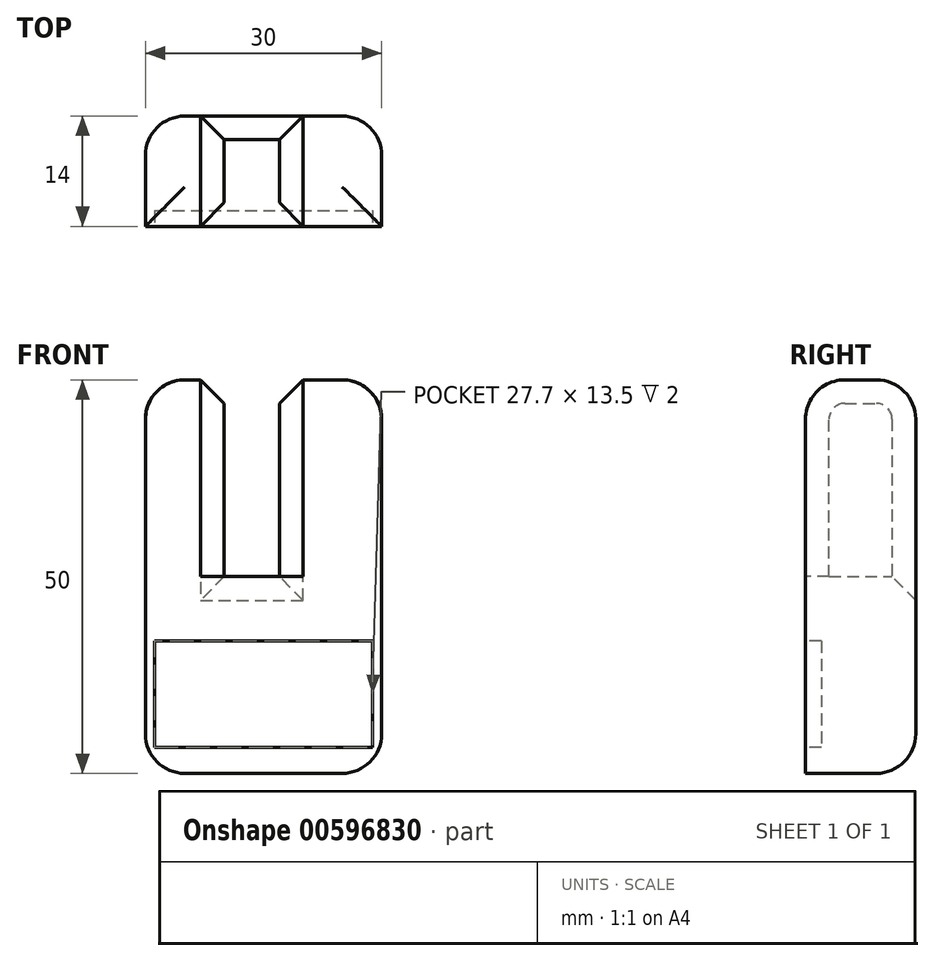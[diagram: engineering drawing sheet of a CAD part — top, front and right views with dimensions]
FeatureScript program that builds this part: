
annotation { "Feature Type Name" : "Feature", "Feature Type Description" : "" }
export const myFeature = defineFeature(function(context is Context, id is Id, definition is map)
    precondition{}
    {
        {
            var Q0;
            Q0=qCreatedBy(makeId("Front.planeOp"),FACE);
            var sketch = newSketch(context, id + "F0", { "sketchPlane" : qUnion([Q0])});
            skLineSegment(sketch, "E0.bottom", {"start": v(-13.28, -20.83) * mm, "end": v(16.72, -20.83) * mm});
            skLineSegment(sketch, "E0.top", {"start": v(-13.28, 29.17) * mm, "end": v(16.72, 29.17) * mm});
            skLineSegment(sketch, "E0.left", {"start": v(-13.28, -20.83) * mm, "end": v(-13.28, 29.17) * mm});
            skLineSegment(sketch, "E0.right", {"start": v(16.72, -20.83) * mm, "end": v(16.72, 29.17) * mm});
            skLineSegment(sketch, "E1.bottom", {"start": v(-3.28, 4.17) * mm, "end": v(3.73, 4.17) * mm});
            skLineSegment(sketch, "E1.top", {"start": v(-3.28, 29.17) * mm, "end": v(3.73, 29.17) * mm});
            skLineSegment(sketch, "E1.left", {"start": v(-3.28, 4.17) * mm, "end": v(-3.28, 29.17) * mm});
            skLineSegment(sketch, "E1.right", {"start": v(3.73, 4.17) * mm, "end": v(3.73, 29.17) * mm});
            skLineSegment(sketch, "E2.bottom", {"start": v(-12.13, -4.12) * mm, "end": v(15.57, -4.12) * mm});
            skLineSegment(sketch, "E2.top", {"start": v(-12.13, -17.62) * mm, "end": v(15.57, -17.62) * mm});
            skLineSegment(sketch, "E2.left", {"start": v(-12.13, -4.12) * mm, "end": v(-12.13, -17.62) * mm});
            skLineSegment(sketch, "E2.right", {"start": v(15.57, -4.12) * mm, "end": v(15.57, -17.62) * mm});
            skSolve(sketch);
        }
        {
            var Q0;
            Q0=makeQuery(id+"F0.imprint","IMPRINT",FACE,{"disambiguationData":[TD([[makeQuery(id+"F0.imprint","IMPRINT",EDGE,{"derivedFrom":sQuery(id+"F0.wireOp",EDGE,"E2.bottom")}),-1.0]])]});
            var Q1;
            Q1=makeQuery(id+"F0.imprint","IMPRINT",FACE,{"disambiguationData":[TD([[makeQuery(id+"F0.imprint","IMPRINT",EDGE,{"derivedFrom":sQuery(id+"F0.wireOp",EDGE,"E0.bottom")}),1.0]])]});
            extrude(context, id + "F1", {"entities" : qUnion([Q0, Q1]), "depth" : 14 * mm, "offsetDistance" : 25 * mm});
        }
        {
            var Q0;
            Q0=makeQuery(id+"F1.opExtrude","CAP_EDGE",EDGE,{"disambiguationData":[OSD([sQuery(id+"F0.wireOp",EDGE,"E0.bottom")])],"isStart":true});
            var Q1;
            Q1=makeQuery(id+"F1.opExtrude","CAP_EDGE",EDGE,{"disambiguationData":[OSD([sQuery(id+"F0.wireOp",EDGE,"E0.left")])],"isStart":true});
            var Q2;
            Q2=makeQuery(id+"F1.opExtrude","CAP_EDGE",EDGE,{"disambiguationData":[OSD([sQuery(id+"F0.wireOp",EDGE,"E0.right")])],"isStart":true});
            var Q3;
            Q3=makeQuery(id+"F1.opExtrude","SWEPT_EDGE",EDGE,{"disambiguationData":[OSD([sQuery(id+"F0.wireOp",EDGE,"E0.bottom"),sQuery(id+"F0.wireOp",EDGE,"E0.right")])]});
            var Q4;
            Q4=makeQuery(id+"F1.opExtrude","SWEPT_EDGE",EDGE,{"disambiguationData":[OSD([sQuery(id+"F0.wireOp",EDGE,"E0.bottom"),sQuery(id+"F0.wireOp",EDGE,"E0.left")])]});
            var Q5;
            {var subQ0=sQuery(id+"F0.wireOp",EDGE,"E0.top");Q5=makeQuery(id+"F1.opExtrude","CAP_EDGE",EDGE,{"disambiguationData":[OSD([subQ0]),TDD([makeQuery(id+"F0.imprint","IMPRINT",EDGE,{"disambiguationData":[TD([[makeQuery(id+"F0.imprint","INTERSECT",VERTEX,{"derivedFrom":[subQ0,sQuery(id+"F0.wireOp",EDGE,"E0.left")]}),-1.0]])],"derivedFrom":subQ0})])],"isStart":true});}
            var Q6;
            {var subQ0=sQuery(id+"F0.wireOp",EDGE,"E0.top");Q6=makeQuery(id+"F1.opExtrude","CAP_EDGE",EDGE,{"disambiguationData":[OSD([subQ0]),TDD([makeQuery(id+"F0.imprint","IMPRINT",EDGE,{"disambiguationData":[TD([[makeQuery(id+"F0.imprint","INTERSECT",VERTEX,{"derivedFrom":[subQ0,sQuery(id+"F0.wireOp",EDGE,"E0.right")]}),1.0]])],"derivedFrom":subQ0})])],"isStart":true});}
            var Q7;
            Q7=makeQuery(id+"F1.opExtrude","SWEPT_EDGE",EDGE,{"disambiguationData":[OSD([sQuery(id+"F0.wireOp",EDGE,"E0.top"),sQuery(id+"F0.wireOp",EDGE,"E0.left")])]});
            var Q8;
            Q8=makeQuery(id+"F1.opExtrude","SWEPT_EDGE",EDGE,{"disambiguationData":[OSD([sQuery(id+"F0.wireOp",EDGE,"E0.top"),sQuery(id+"F0.wireOp",EDGE,"E0.right")])]});
            var Q9;
            {var subQ0=sQuery(id+"F0.wireOp",EDGE,"E0.top");Q9=makeQuery(id+"F1.opExtrude","CAP_EDGE",EDGE,{"disambiguationData":[OSD([subQ0]),TDD([makeQuery(id+"F0.imprint","IMPRINT",EDGE,{"disambiguationData":[TD([[makeQuery(id+"F0.imprint","INTERSECT",VERTEX,{"derivedFrom":[subQ0,sQuery(id+"F0.wireOp",EDGE,"E0.right")]}),1.0]])],"derivedFrom":subQ0})])],"isStart":false});}
            var Q10;
            {var subQ0=sQuery(id+"F0.wireOp",EDGE,"E0.top");Q10=makeQuery(id+"F1.opExtrude","CAP_EDGE",EDGE,{"disambiguationData":[OSD([subQ0]),TDD([makeQuery(id+"F0.imprint","IMPRINT",EDGE,{"disambiguationData":[TD([[makeQuery(id+"F0.imprint","INTERSECT",VERTEX,{"derivedFrom":[subQ0,sQuery(id+"F0.wireOp",EDGE,"E0.left")]}),-1.0]])],"derivedFrom":subQ0})])],"isStart":false});}
            fillet(context, id + "F2", {"entities" : qUnion([Q0, Q1, Q2, Q3, Q4, Q5, Q6, Q7, Q8, Q9, Q10]), "radius" : 5 * mm, "tangentPropagation" : true, "allowEdgeOverflow" : false});
        }
        {
            var Q0;
            Q0=makeQuery(id+"F0.imprint","IMPRINT",FACE,{"disambiguationData":[TD([[makeQuery(id+"F0.imprint","IMPRINT",EDGE,{"derivedFrom":sQuery(id+"F0.wireOp",EDGE,"E0.bottom")}),1.0]])]});
            var sketch = newSketch(context, id + "F3", { "sketchPlane" : qUnion([Q0])});
            skText(sketch, "E3", { "text": "VERBIO", "fontName": "OpenSans-Bold.ttf"});
            const initialGuessF3  = {"E3": [0.01147, -0.0047, -1, 0, 0.00392]};
            skSetInitialGuess(sketch, initialGuessF3);
            skSolve(sketch);
        }
        {
            var Q0;
            Q0=makeQuery(id+"F1.opExtrude","CAP_FACE",FACE,{"disambiguationData":[OSD([sQuery(id+"F0.wireOp",EDGE,"E0.bottom"),sQuery(id+"F0.wireOp",EDGE,"E0.top"),sQuery(id+"F0.wireOp",EDGE,"E0.left"),sQuery(id+"F0.wireOp",EDGE,"E0.right"),sQuery(id+"F0.wireOp",EDGE,"E1.bottom"),sQuery(id+"F0.wireOp",EDGE,"E1.left"),sQuery(id+"F0.wireOp",EDGE,"E1.right")])],"isStart":false});
            var sketch = newSketch(context, id + "F4", { "sketchPlane" : qUnion([Q0])});
            skPoint(sketch, "E4.firstSnap0", {"position": v(-11.82, -19.36) * mm});
            skLineSegment(sketch, "E5.bottom", {"start": v(-12.1, -4.01) * mm, "end": v(15.6, -4.01) * mm});
            skLineSegment(sketch, "E5.top", {"start": v(-12.1, -17.51) * mm, "end": v(15.6, -17.51) * mm});
            skLineSegment(sketch, "E5.left", {"start": v(-12.1, -4.01) * mm, "end": v(-12.1, -17.51) * mm});
            skLineSegment(sketch, "E5.right", {"start": v(15.6, -4.01) * mm, "end": v(15.6, -17.51) * mm});
            skSolve(sketch);
        }
        {
            var Q0;
            Q0 = qSketchRegion(id + "F4", true);
            extrude(context, id + "F5", {"entities" : qUnion([Q0]), "operationType" : NewBodyOperationType.REMOVE, "oppositeDirection" : true, "depth" : 2 * mm, "offsetDistance" : 25 * mm});
        }
        {
            var Q0;
            Q0=makeQuery(id+"F1.opExtrude","CAP_EDGE",EDGE,{"disambiguationData":[OSD([sQuery(id+"F0.wireOp",EDGE,"E1.left")])],"isStart":true});
            var Q1;
            Q1=makeQuery(id+"F1.opExtrude","CAP_EDGE",EDGE,{"disambiguationData":[OSD([sQuery(id+"F0.wireOp",EDGE,"E1.right")])],"isStart":true});
            var Q2;
            Q2=makeQuery(id+"F1.opExtrude","CAP_EDGE",EDGE,{"disambiguationData":[OSD([sQuery(id+"F0.wireOp",EDGE,"E1.bottom")])],"isStart":true});
            chamfer(context, id + "F6", {"entities" : qUnion([Q0, Q1, Q2]), "width" : 3 * mm, "tangentPropagation" : true});
        }
    });
